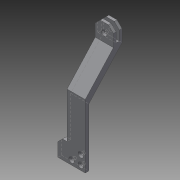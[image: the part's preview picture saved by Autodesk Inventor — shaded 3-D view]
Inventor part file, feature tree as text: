
AUTODESK INVENTOR PART (.ipt)
format: ipt  version: 2015 (Build 190159000, 159)  size: 186,880 bytes
history: native  units: mm
features: sketch x10, extrude x8, hole x2, chamfer x2
ambient origin geometry x8: Origin, YZ Plane, XZ Plane, XY Plane, X Axis, Y Axis, Z Axis, Center Point
bodies: Solid1 (feature_tree)
feature tree (22):
  extrude  "Extrusion1"  Depth=4.0mm
  extrude  "Extrusion2"  Depth=103.0mm
  hole  "Hole1"  [1 undecoded]
  chamfer  "Chamfer1"  Distance=5.0mm Angle=45.0deg
  extrude  "Extrusion3"  Depth=20.0mm TaperAngle=0.0deg
  extrude  "Extrusion4"  Depth=4.0mm
  extrude  "Extrusion5"  Depth=30.0mm
  extrude  "Extrusion6"  Depth=20.0mm TaperAngle=0.0deg
  extrude  "Extrusion7"  Depth=3.0mm
  extrude  "Extrusion8"  Depth=3.0mm
  hole  "Hole2"  [1 undecoded]
  chamfer  "Chamfer2"  Distance=3.0mm
  sketch  "Sketch1"  dims[d0=30.0mm d1=4.0mm]
  sketch  "Sketch2"  dims[d2=20.0mm d3=0.0mm d4=103.0mm]
  sketch  "Sketch3"  dims[d5=20.0mm d6=10.0mm d7=0.0mm]
  sketch  "Sketch4"  dims[d8=5.0mm]
  sketch  "Sketch5"  dims[d9=5.0mm]
  sketch  "Sketch6"  dims[d10=5.0mm]
  sketch  "Sketch7"  dims[d11=5.0mm]
  sketch  "Sketch8"  dims[d12=5.0mm]
  sketch  "Sketch9"  dims[d13=10.0mm]
  sketch  "Sketch10"  dims[d14=3.0mm d15=6.0mm d16=6.0mm d17=2.0mm d18=90.0deg d19=8.0mm d20=20.594885mm d21=5.0mm d22=2.0mm d23=45.0deg d24=20.0mm d25=0.0mm d26=4.0mm d27=30.0mm d28=20.0mm d29=0.0mm d30=15.0mm d31=3.0mm d32=3.5mm d33=3.0mm d34=4.0mm d35=20.0mm d36=0.0mm d37=1.0mm d38=20.0mm d39=0.0mm d40=50.0mm d41=20.0mm d42=0.0mm d43=20.0mm d44=0.0mm d45=6.0mm d46=3.0mm d47=6.0mm d48=6.0mm d49=2.0mm d50=90.0deg d51=15.0mm d52=20.594885mm d53=5.5mm d54=2.0mm d55=45.0deg]
note: 2 required parameter values undecoded (feature->parameter linkage not recoverable at this tier; creation-order binding heuristic only, values carry confidence <= 0.55)
